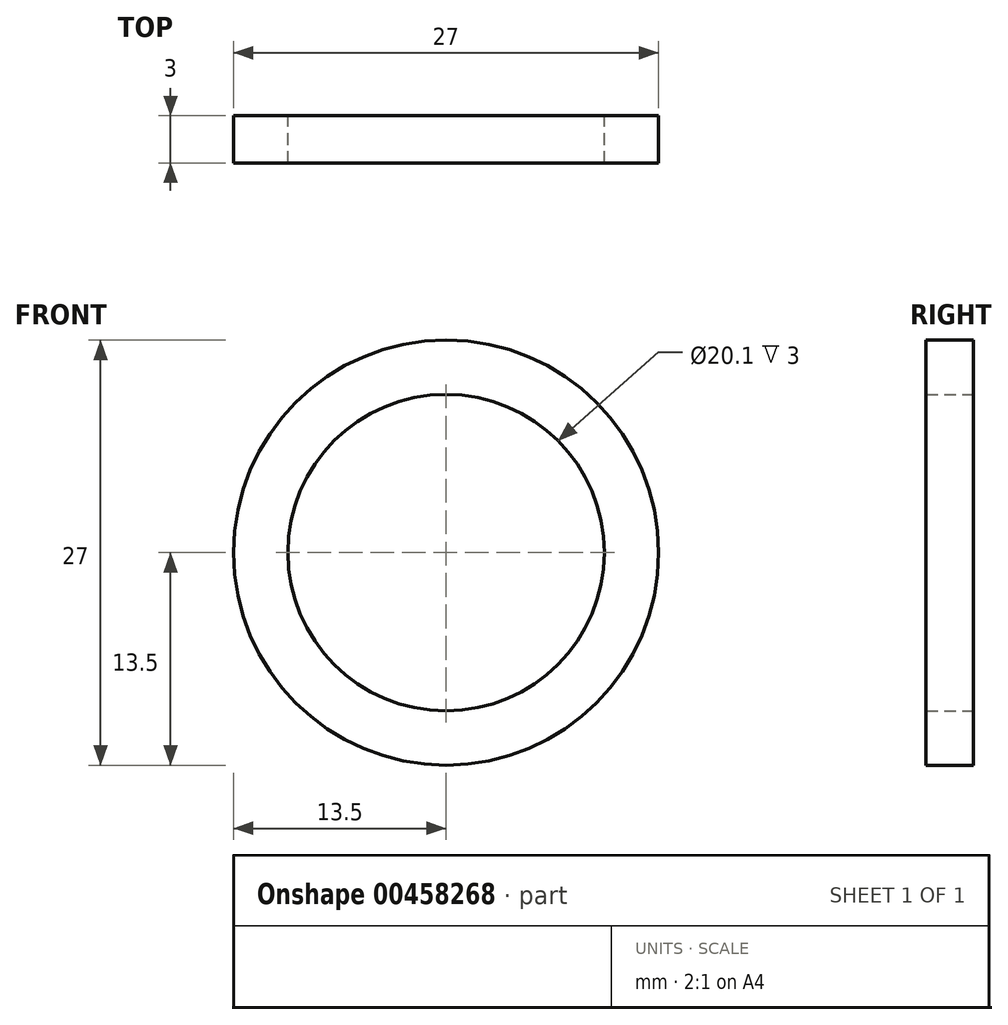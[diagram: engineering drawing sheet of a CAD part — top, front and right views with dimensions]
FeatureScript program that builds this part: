
annotation { "Feature Type Name" : "Feature", "Feature Type Description" : "" }
export const myFeature = defineFeature(function(context is Context, id is Id, definition is map)
    precondition{}
    {
        {
            var Q0;
            Q0=qCreatedBy(makeId("Front.planeOp"),FACE);
            var sketch = newSketch(context, id + "F0", { "sketchPlane" : qUnion([Q0])});
            skCircle(sketch, "E0", {"center": v(0, 0) * mm, "radius": 10.05 * mm});
            skCircle(sketch, "E1", {"center": v(0, 0) * mm, "radius": 13.5 * mm});
            skSolve(sketch);
        }
        {
            var Q0;
            Q0=makeQuery(id+"F0.imprint","IMPRINT",FACE,{"disambiguationData":[TD([[makeQuery(id+"F0.imprint","IMPRINT",EDGE,{"derivedFrom":sQuery(id+"F0.wireOp",EDGE,"E0")}),-1.0]])]});
            extrude(context, id + "F1", {"entities" : qUnion([Q0]), "depth" : 3 * mm});
        }
    });
